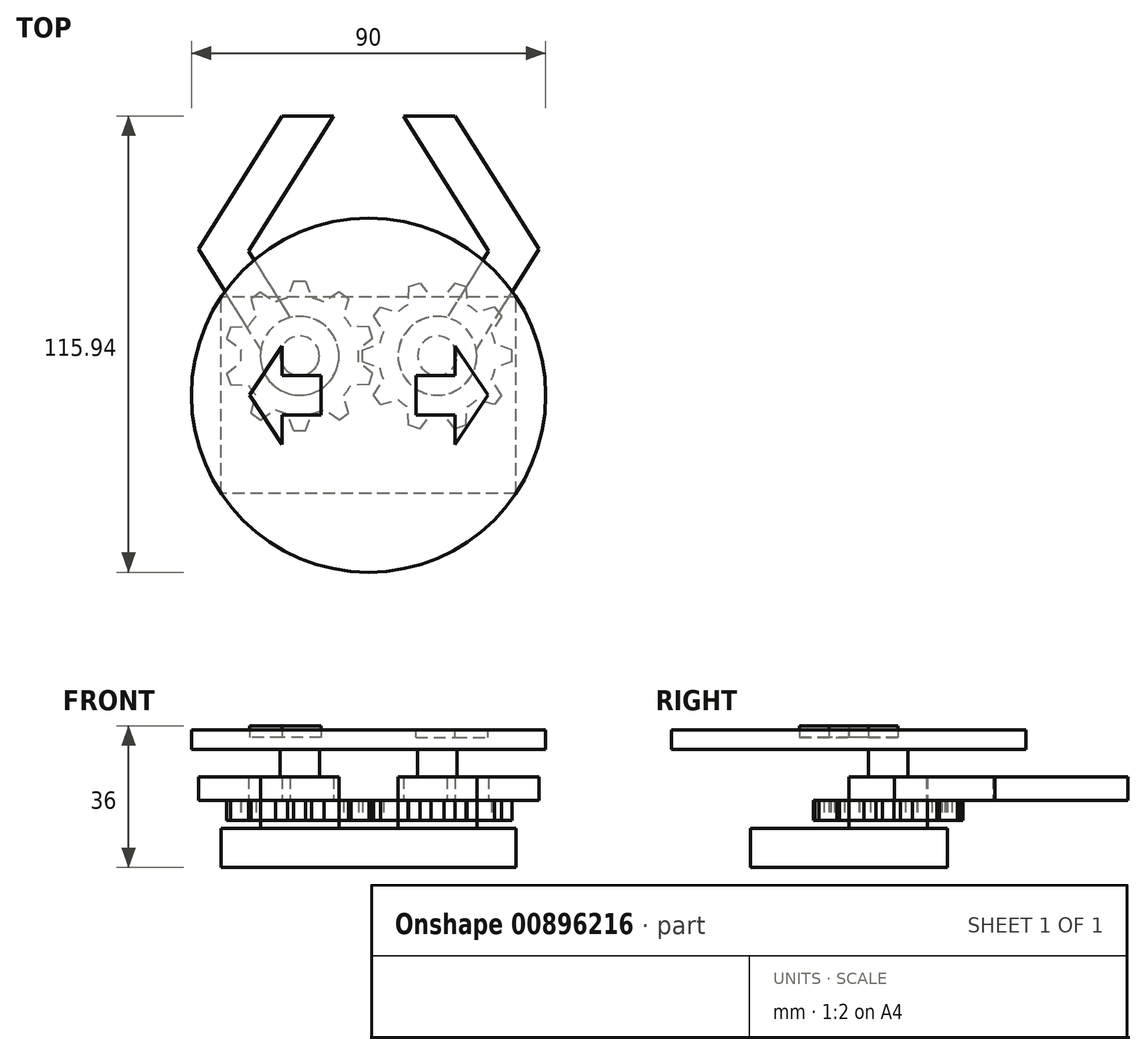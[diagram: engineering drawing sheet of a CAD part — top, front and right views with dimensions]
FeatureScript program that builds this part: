
annotation { "Feature Type Name" : "Feature", "Feature Type Description" : "" }
export const myFeature = defineFeature(function(context is Context, id is Id, definition is map)
    precondition{}
    {
        {
            var Q0;
            Q0=qCreatedBy(makeId("Top.planeOp"),FACE);
            var sketch = newSketch(context, id + "F0", { "sketchPlane" : qUnion([Q0])});
            skLineSegment(sketch, "E0.bottom", {"start": v(37.5, -25) * mm, "end": v(-37.5, -25) * mm});
            skLineSegment(sketch, "E0.top", {"start": v(37.5, 25) * mm, "end": v(-37.5, 25) * mm});
            skLineSegment(sketch, "E0.left", {"start": v(37.5, -25) * mm, "end": v(37.5, 25) * mm});
            skLineSegment(sketch, "E0.right", {"start": v(-37.5, -25) * mm, "end": v(-37.5, 25) * mm});
            skPoint(sketch, "E0.middle", {"position": v(0, 0) * mm});
            skSolve(sketch);
        }
        {
            var Q0;
            Q0 = qSketchRegion(id + "F0", true);
            extrude(context, id + "F1", {"entities" : qUnion([Q0]), "depth" : 10 * mm, "offsetDistance" : 25 * mm});
        }
        {
            var Q0;
            Q0=makeQuery(id+"F1.opExtrude","CAP_FACE",FACE,{"disambiguationData":[OSD([sQuery(id+"F0.wireOp",EDGE,"E0.bottom"),sQuery(id+"F0.wireOp",EDGE,"E0.top"),sQuery(id+"F0.wireOp",EDGE,"E0.left"),sQuery(id+"F0.wireOp",EDGE,"E0.right")])],"isStart":false});
            var sketch = newSketch(context, id + "F2", { "sketchPlane" : qUnion([Q0])});
            skPoint(sketch, "E1.centerSnap0", {"position": v(-37.5, 0) * mm});
            skCircle(sketch, "E2", {"center": v(-17.5, 10) * mm, "radius": 10 * mm});
            skCircle(sketch, "E3", {"center": v(-17.5, 10) * mm, "radius": 3.5 * mm});
            skCircle(sketch, "E4", {"center": v(17.5, 10) * mm, "radius": 3.5 * mm});
            skCircle(sketch, "E5", {"center": v(17.5, 10) * mm, "radius": 10 * mm});
            skSolve(sketch);
        }
        {
            var Q0;
            Q0 = qSketchRegion(id + "F2", true);
            extrude(context, id + "F3", {"entities" : qUnion([Q0]), "operationType" : NewBodyOperationType.ADD, "depth" : 2 * mm, "offsetDistance" : 25 * mm});
        }
        {
            var Q0;
            Q0=makeQuery(id+"F3.boolean.opBoolean","SPLIT",FACE,{"disambiguationData":[TD([makeQuery(id+"F3.opExtrude","SWEPT_FACE",FACE,{"disambiguationData":[OSD([sQuery(id+"F2.wireOp",EDGE,"E3")])]})])],"derivedFrom":makeQuery(id+"F1.opExtrude","CAP_FACE",FACE,{"disambiguationData":[OSD([sQuery(id+"F0.wireOp",EDGE,"E0.bottom"),sQuery(id+"F0.wireOp",EDGE,"E0.top"),sQuery(id+"F0.wireOp",EDGE,"E0.left"),sQuery(id+"F0.wireOp",EDGE,"E0.right")])],"isStart":false})});
            extrude(context, id + "F4", {"entities" : qUnion([Q0]), "depth" : 20 * mm, "offsetDistance" : 25 * mm});
        }
        {
            var Q0;
            Q0=makeQuery(id+"F3.boolean.opBoolean","SPLIT",FACE,{"disambiguationData":[TD([makeQuery(id+"F3.opExtrude","SWEPT_FACE",FACE,{"disambiguationData":[OSD([sQuery(id+"F2.wireOp",EDGE,"E4")])]})])],"derivedFrom":makeQuery(id+"F1.opExtrude","CAP_FACE",FACE,{"disambiguationData":[OSD([sQuery(id+"F0.wireOp",EDGE,"E0.bottom"),sQuery(id+"F0.wireOp",EDGE,"E0.top"),sQuery(id+"F0.wireOp",EDGE,"E0.left"),sQuery(id+"F0.wireOp",EDGE,"E0.right")])],"isStart":false})});
            extrude(context, id + "F5", {"entities" : qUnion([Q0]), "depth" : 20 * mm, "offsetDistance" : 25 * mm});
        }
        {
            var Q0;
            Q0=makeQuery(id+"F3.opExtrude","CAP_FACE",FACE,{"disambiguationData":[OSD([sQuery(id+"F2.wireOp",EDGE,"E2"),sQuery(id+"F2.wireOp",EDGE,"E3")])],"isStart":false});
            var sketch = newSketch(context, id + "F6", { "sketchPlane" : qUnion([Q0])});
            skCircle(sketch, "E6", {"center": v(-17.5, 10) * mm, "radius": 15 * mm});
            skLineSegment(sketch, "E7", {"start": v(-17.5, 10) * mm, "end": v(-17.5, 25) * mm, "construction": true});
            skLineSegment(sketch, "E8", {"start": v(-17.5, 29) * mm, "end": v(-16, 29) * mm});
            skLineSegment(sketch, "E9", {"start": v(-16, 29) * mm, "end": v(-14.43, 24.68) * mm});
            skLineSegment(sketch, "E10.MirrorCS", {"start": v(-17.5, 29) * mm, "end": v(-19, 29) * mm});
            skLineSegment(sketch, "E11.MirrorCS", {"start": v(-19, 29) * mm, "end": v(-20.57, 24.68) * mm});
            skLineSegment(sketch, "E12.1.0", {"start": v(-29.88, 24.49) * mm, "end": v(-28.61, 20.07) * mm});
            skLineSegment(sketch, "E12.1.1", {"start": v(-28.67, 25.37) * mm, "end": v(-29.88, 24.49) * mm});
            skLineSegment(sketch, "E12.1.2", {"start": v(-28.67, 25.37) * mm, "end": v(-27.45, 26.25) * mm});
            skLineSegment(sketch, "E12.1.3", {"start": v(-27.45, 26.25) * mm, "end": v(-23.64, 23.68) * mm});
            skLineSegment(sketch, "E12.2.0", {"start": v(-36.03, 14.44) * mm, "end": v(-32.41, 11.62) * mm});
            skLineSegment(sketch, "E12.2.1", {"start": v(-35.57, 15.87) * mm, "end": v(-36.03, 14.44) * mm});
            skLineSegment(sketch, "E12.2.2", {"start": v(-35.57, 15.87) * mm, "end": v(-35.1, 17.3) * mm});
            skLineSegment(sketch, "E12.2.3", {"start": v(-35.1, 17.3) * mm, "end": v(-30.51, 17.46) * mm});
            skLineSegment(sketch, "E13.2.3.0", {"start": v(-35.1, 2.7) * mm, "end": v(-30.51, 2.54) * mm});
            skLineSegment(sketch, "E13.3.3.0", {"start": v(-35.57, 4.13) * mm, "end": v(-35.1, 2.7) * mm});
            skLineSegment(sketch, "E13.6.3.0", {"start": v(-35.57, 4.13) * mm, "end": v(-36.03, 5.56) * mm});
            skLineSegment(sketch, "E13.9.3.0", {"start": v(-36.03, 5.56) * mm, "end": v(-32.41, 8.38) * mm});
            skLineSegment(sketch, "E13.2.4.0", {"start": v(-27.45, -6.25) * mm, "end": v(-23.64, -3.68) * mm});
            skLineSegment(sketch, "E13.3.4.0", {"start": v(-28.67, -5.37) * mm, "end": v(-27.45, -6.25) * mm});
            skLineSegment(sketch, "E13.6.4.0", {"start": v(-28.67, -5.37) * mm, "end": v(-29.88, -4.49) * mm});
            skLineSegment(sketch, "E13.9.4.0", {"start": v(-29.88, -4.49) * mm, "end": v(-28.61, -0.07) * mm});
            skLineSegment(sketch, "E14.2.5.0", {"start": v(-16, -9) * mm, "end": v(-14.43, -4.68) * mm});
            skLineSegment(sketch, "E14.3.5.0", {"start": v(-17.5, -9) * mm, "end": v(-16, -9) * mm});
            skLineSegment(sketch, "E14.6.5.0", {"start": v(-17.5, -9) * mm, "end": v(-19, -9) * mm});
            skLineSegment(sketch, "E14.9.5.0", {"start": v(-19, -9) * mm, "end": v(-20.57, -4.68) * mm});
            skLineSegment(sketch, "E14.2.6.0", {"start": v(-5.12, -4.49) * mm, "end": v(-6.39, -0.07) * mm});
            skLineSegment(sketch, "E14.3.6.0", {"start": v(-6.33, -5.37) * mm, "end": v(-5.12, -4.49) * mm});
            skLineSegment(sketch, "E14.6.6.0", {"start": v(-6.33, -5.37) * mm, "end": v(-7.55, -6.25) * mm});
            skLineSegment(sketch, "E14.9.6.0", {"start": v(-7.55, -6.25) * mm, "end": v(-11.36, -3.68) * mm});
            skLineSegment(sketch, "E14.2.7.0", {"start": v(1.03, 5.56) * mm, "end": v(-2.59, 8.38) * mm});
            skLineSegment(sketch, "E14.3.7.0", {"start": v(0.57, 4.13) * mm, "end": v(1.03, 5.56) * mm});
            skLineSegment(sketch, "E14.6.7.0", {"start": v(0.57, 4.13) * mm, "end": v(0.1, 2.7) * mm});
            skLineSegment(sketch, "E14.9.7.0", {"start": v(0.1, 2.7) * mm, "end": v(-4.49, 2.54) * mm});
            skLineSegment(sketch, "E14.2.8.0", {"start": v(0.1, 17.3) * mm, "end": v(-4.49, 17.46) * mm});
            skLineSegment(sketch, "E14.3.8.0", {"start": v(0.57, 15.87) * mm, "end": v(0.1, 17.3) * mm});
            skLineSegment(sketch, "E14.6.8.0", {"start": v(0.57, 15.87) * mm, "end": v(1.03, 14.44) * mm});
            skLineSegment(sketch, "E14.9.8.0", {"start": v(1.03, 14.44) * mm, "end": v(-2.59, 11.62) * mm});
            skLineSegment(sketch, "E14.2.9.0", {"start": v(-7.55, 26.25) * mm, "end": v(-11.36, 23.68) * mm});
            skLineSegment(sketch, "E14.3.9.0", {"start": v(-6.33, 25.37) * mm, "end": v(-7.55, 26.25) * mm});
            skLineSegment(sketch, "E14.6.9.0", {"start": v(-6.33, 25.37) * mm, "end": v(-5.12, 24.49) * mm});
            skLineSegment(sketch, "E14.9.9.0", {"start": v(-5.12, 24.49) * mm, "end": v(-6.39, 20.07) * mm});
            skSolve(sketch);
        }
        {
            var Q0;
            Q0 = qSketchRegion(id + "F6", true);
            extrude(context, id + "F7", {"entities" : qUnion([Q0]), "operationType" : NewBodyOperationType.ADD, "depth" : 5 * mm, "offsetDistance" : 25 * mm});
        }
        {
            var Q0;
            Q0=makeQuery(id+"F3.opExtrude","CAP_FACE",FACE,{"disambiguationData":[OSD([sQuery(id+"F2.wireOp",EDGE,"E4"),sQuery(id+"F2.wireOp",EDGE,"E5")])],"isStart":false});
            var sketch = newSketch(context, id + "F8", { "sketchPlane" : qUnion([Q0])});
            skCircle(sketch, "E15", {"center": v(17.5, 10) * mm, "radius": 15 * mm});
            skLineSegment(sketch, "E16", {"start": v(17.5, 10) * mm, "end": v(2.5, 10) * mm, "construction": true});
            skLineSegment(sketch, "E17", {"start": v(-1.5, 10) * mm, "end": v(-1.5, 11.5) * mm});
            skLineSegment(sketch, "E18", {"start": v(-1.5, 11.5) * mm, "end": v(2.82, 13.07) * mm});
            skLineSegment(sketch, "E19.MirrorCS", {"start": v(-1.5, 10) * mm, "end": v(-1.5, 8.5) * mm});
            skLineSegment(sketch, "E20.MirrorCS", {"start": v(-1.5, 8.5) * mm, "end": v(2.82, 6.93) * mm});
            skLineSegment(sketch, "E21.1.0", {"start": v(2.13, -1.17) * mm, "end": v(1.25, 0.05) * mm});
            skLineSegment(sketch, "E21.1.1", {"start": v(1.25, 0.05) * mm, "end": v(3.82, 3.86) * mm});
            skLineSegment(sketch, "E21.1.2", {"start": v(2.13, -1.17) * mm, "end": v(3.01, -2.38) * mm});
            skLineSegment(sketch, "E21.1.3", {"start": v(3.01, -2.38) * mm, "end": v(7.43, -1.11) * mm});
            skLineSegment(sketch, "E21.2.0", {"start": v(11.63, -8.07) * mm, "end": v(10.2, -7.6) * mm});
            skLineSegment(sketch, "E21.2.1", {"start": v(10.2, -7.6) * mm, "end": v(10.04, -3.01) * mm});
            skLineSegment(sketch, "E21.2.2", {"start": v(11.63, -8.07) * mm, "end": v(13.06, -8.53) * mm});
            skLineSegment(sketch, "E21.2.3", {"start": v(13.06, -8.53) * mm, "end": v(15.88, -4.91) * mm});
            skLineSegment(sketch, "E22.1.3.0", {"start": v(23.37, -8.07) * mm, "end": v(21.94, -8.53) * mm});
            skLineSegment(sketch, "E22.3.3.0", {"start": v(21.94, -8.53) * mm, "end": v(19.12, -4.91) * mm});
            skLineSegment(sketch, "E22.6.3.0", {"start": v(23.37, -8.07) * mm, "end": v(24.8, -7.6) * mm});
            skLineSegment(sketch, "E22.9.3.0", {"start": v(24.8, -7.6) * mm, "end": v(24.96, -3.01) * mm});
            skLineSegment(sketch, "E22.1.4.0", {"start": v(32.87, -1.17) * mm, "end": v(31.99, -2.38) * mm});
            skLineSegment(sketch, "E22.3.4.0", {"start": v(31.99, -2.38) * mm, "end": v(27.57, -1.11) * mm});
            skLineSegment(sketch, "E22.6.4.0", {"start": v(32.87, -1.17) * mm, "end": v(33.75, 0.05) * mm});
            skLineSegment(sketch, "E22.9.4.0", {"start": v(33.75, 0.05) * mm, "end": v(31.18, 3.86) * mm});
            skLineSegment(sketch, "E22.1.5.0", {"start": v(36.5, 10) * mm, "end": v(36.5, 8.5) * mm});
            skLineSegment(sketch, "E22.3.5.0", {"start": v(36.5, 8.5) * mm, "end": v(32.18, 6.93) * mm});
            skLineSegment(sketch, "E22.6.5.0", {"start": v(36.5, 10) * mm, "end": v(36.5, 11.5) * mm});
            skLineSegment(sketch, "E22.9.5.0", {"start": v(36.5, 11.5) * mm, "end": v(32.18, 13.07) * mm});
            skLineSegment(sketch, "E22.1.6.0", {"start": v(32.87, 21.17) * mm, "end": v(33.75, 19.95) * mm});
            skLineSegment(sketch, "E22.3.6.0", {"start": v(33.75, 19.95) * mm, "end": v(31.18, 16.14) * mm});
            skLineSegment(sketch, "E22.6.6.0", {"start": v(32.87, 21.17) * mm, "end": v(31.99, 22.38) * mm});
            skLineSegment(sketch, "E22.9.6.0", {"start": v(31.99, 22.38) * mm, "end": v(27.57, 21.11) * mm});
            skLineSegment(sketch, "E22.1.7.0", {"start": v(23.37, 28.07) * mm, "end": v(24.8, 27.6) * mm});
            skLineSegment(sketch, "E22.3.7.0", {"start": v(24.8, 27.6) * mm, "end": v(24.96, 23.01) * mm});
            skLineSegment(sketch, "E22.6.7.0", {"start": v(23.37, 28.07) * mm, "end": v(21.94, 28.53) * mm});
            skLineSegment(sketch, "E22.9.7.0", {"start": v(21.94, 28.53) * mm, "end": v(19.12, 24.91) * mm});
            skLineSegment(sketch, "E22.1.8.0", {"start": v(11.63, 28.07) * mm, "end": v(13.06, 28.53) * mm});
            skLineSegment(sketch, "E22.3.8.0", {"start": v(13.06, 28.53) * mm, "end": v(15.88, 24.91) * mm});
            skLineSegment(sketch, "E22.6.8.0", {"start": v(11.63, 28.07) * mm, "end": v(10.2, 27.6) * mm});
            skLineSegment(sketch, "E22.9.8.0", {"start": v(10.2, 27.6) * mm, "end": v(10.04, 23.01) * mm});
            skLineSegment(sketch, "E22.1.9.0", {"start": v(2.13, 21.17) * mm, "end": v(3.01, 22.38) * mm});
            skLineSegment(sketch, "E22.3.9.0", {"start": v(3.01, 22.38) * mm, "end": v(7.43, 21.11) * mm});
            skLineSegment(sketch, "E22.6.9.0", {"start": v(2.13, 21.17) * mm, "end": v(1.25, 19.95) * mm});
            skLineSegment(sketch, "E22.9.9.0", {"start": v(1.25, 19.95) * mm, "end": v(3.82, 16.14) * mm});
            skSolve(sketch);
        }
        {
            var Q0;
            Q0 = qSketchRegion(id + "F8", true);
            extrude(context, id + "F9", {"entities" : qUnion([Q0]), "operationType" : NewBodyOperationType.ADD, "depth" : 5 * mm, "offsetDistance" : 25 * mm});
        }
        {
            var Q0;
            Q0=makeQuery(id+"F7.opExtrude","CAP_FACE",FACE,{"disambiguationData":[OSD([sQuery(id+"F6.wireOp",EDGE,"E6"),sQuery(id+"F6.wireOp",EDGE,"E8"),sQuery(id+"F6.wireOp",EDGE,"E9"),sQuery(id+"F6.wireOp",EDGE,"E10.MirrorCS"),sQuery(id+"F6.wireOp",EDGE,"E11.MirrorCS"),sQuery(id+"F6.wireOp",EDGE,"E12.1.0"),sQuery(id+"F6.wireOp",EDGE,"E12.1.1"),sQuery(id+"F6.wireOp",EDGE,"E12.1.2"),sQuery(id+"F6.wireOp",EDGE,"E12.1.3"),sQuery(id+"F6.wireOp",EDGE,"E12.2.0"),sQuery(id+"F6.wireOp",EDGE,"E12.2.1"),sQuery(id+"F6.wireOp",EDGE,"E12.2.2"),sQuery(id+"F6.wireOp",EDGE,"E12.2.3"),sQuery(id+"F6.wireOp",EDGE,"E13.2.3.0"),sQuery(id+"F6.wireOp",EDGE,"E13.3.3.0"),sQuery(id+"F6.wireOp",EDGE,"E13.6.3.0"),sQuery(id+"F6.wireOp",EDGE,"E13.9.3.0"),sQuery(id+"F6.wireOp",EDGE,"E13.2.4.0"),sQuery(id+"F6.wireOp",EDGE,"E13.3.4.0"),sQuery(id+"F6.wireOp",EDGE,"E13.6.4.0"),sQuery(id+"F6.wireOp",EDGE,"E13.9.4.0"),sQuery(id+"F6.wireOp",EDGE,"E14.2.5.0"),sQuery(id+"F6.wireOp",EDGE,"E14.3.5.0"),sQuery(id+"F6.wireOp",EDGE,"E14.6.5.0"),sQuery(id+"F6.wireOp",EDGE,"E14.9.5.0"),sQuery(id+"F6.wireOp",EDGE,"E14.2.6.0"),sQuery(id+"F6.wireOp",EDGE,"E14.3.6.0"),sQuery(id+"F6.wireOp",EDGE,"E14.6.6.0"),sQuery(id+"F6.wireOp",EDGE,"E14.9.6.0"),sQuery(id+"F6.wireOp",EDGE,"E14.2.7.0"),sQuery(id+"F6.wireOp",EDGE,"E14.3.7.0"),sQuery(id+"F6.wireOp",EDGE,"E14.6.7.0"),sQuery(id+"F6.wireOp",EDGE,"E14.9.7.0"),sQuery(id+"F6.wireOp",EDGE,"E14.2.8.0"),sQuery(id+"F6.wireOp",EDGE,"E14.3.8.0"),sQuery(id+"F6.wireOp",EDGE,"E14.6.8.0"),sQuery(id+"F6.wireOp",EDGE,"E14.9.8.0"),sQuery(id+"F6.wireOp",EDGE,"E14.2.9.0"),sQuery(id+"F6.wireOp",EDGE,"E14.3.9.0"),sQuery(id+"F6.wireOp",EDGE,"E14.6.9.0"),sQuery(id+"F6.wireOp",EDGE,"E14.9.9.0")])],"isStart":false});
            var sketch = newSketch(context, id + "F10", { "sketchPlane" : qUnion([Q0])});
            skCircle(sketch, "E23.0", {"center": v(-17.5, 10) * mm, "radius": 3.5 * mm});
            skCircle(sketch, "E24.0", {"center": v(-17.5, 10) * mm, "radius": 10 * mm});
            skLineSegment(sketch, "E25", {"start": v(-27.36, 11.64) * mm, "end": v(-43.25, 37.1) * mm});
            skLineSegment(sketch, "E26", {"start": v(-43.25, 37.1) * mm, "end": v(-21.93, 70.94) * mm});
            skLineSegment(sketch, "E27", {"start": v(-21.93, 70.94) * mm, "end": v(-8.93, 70.94) * mm});
            skLineSegment(sketch, "E28", {"start": v(-8.93, 70.94) * mm, "end": v(-30.51, 36.67) * mm});
            skLineSegment(sketch, "E29", {"start": v(-30.51, 36.67) * mm, "end": v(-19.93, 19.7) * mm});
            skSolve(sketch);
        }
        {
            var Q0;
            Q0 = qSketchRegion(id + "F10", true);
            extrude(context, id + "F11", {"entities" : qUnion([Q0]), "depth" : 6 * mm, "offsetDistance" : 25 * mm});
        }
        {
            var Q0;
            Q0=makeQuery(id+"F11.opExtrude","SWEPT_BODY",BODY,{"disambiguationData":[OSD([sQuery(id+"F10.wireOp",EDGE,"E23.0"),sQuery(id+"F10.wireOp",EDGE,"E24.0"),sQuery(id+"F10.wireOp",EDGE,"E25"),sQuery(id+"F10.wireOp",EDGE,"E26"),sQuery(id+"F10.wireOp",EDGE,"E27"),sQuery(id+"F10.wireOp",EDGE,"E28"),sQuery(id+"F10.wireOp",EDGE,"E29")])]});
            var Q1;
            Q1=qCreatedBy(makeId("Right.planeOp"),FACE);
            mirror(context, id + "F12", {"entities" : qUnion([Q0]), "mirrorPlane" : qUnion([Q1])});
        }
        {
            var Q0;
            Q0=makeQuery(id+"F4.opExtrude","CAP_FACE",FACE,{"disambiguationData":[OSD([sQuery(id+"F0.wireOp",EDGE,"E0.bottom"),sQuery(id+"F0.wireOp",EDGE,"E0.top"),sQuery(id+"F0.wireOp",EDGE,"E0.left"),sQuery(id+"F0.wireOp",EDGE,"E0.right")])],"isStart":false});
            var sketch = newSketch(context, id + "F13", { "sketchPlane" : qUnion([Q0])});
            skCircle(sketch, "E30", {"center": v(0, 0) * mm, "radius": 45 * mm});
            skSolve(sketch);
        }
        {
            var Q0;
            Q0 = qSketchRegion(id + "F13", true);
            extrude(context, id + "F14", {"entities" : qUnion([Q0]), "depth" : 5 * mm, "offsetDistance" : 25 * mm});
        }
        {
            var Q0;
            Q0=makeQuery(id+"F14.opExtrude","CAP_FACE",FACE,{"disambiguationData":[OSD([sQuery(id+"F13.wireOp",EDGE,"E30")])],"isStart":true});
            var sketch = newSketch(context, id + "F15", { "sketchPlane" : qUnion([Q0])});
            skCircle(sketch, "E31.0", {"center": v(-17.5, -10) * mm, "radius": 3.5 * mm});
            skCircle(sketch, "E32.0", {"center": v(17.5, -10) * mm, "radius": 3.5 * mm});
            skCircle(sketch, "E33", {"center": v(-17.5, -10) * mm, "radius": 5 * mm});
            skCircle(sketch, "E34", {"center": v(17.5, -10) * mm, "radius": 5 * mm});
            skSolve(sketch);
        }
        {
            var Q0;
            Q0=makeQuery(id+"F15.imprint","IMPRINT",FACE,{"disambiguationData":[TD([[makeQuery(id+"F15.imprint","IMPRINT",EDGE,{"derivedFrom":sQuery(id+"F15.wireOp",EDGE,"E31.0")}),-1.0]])]});
            var Q1;
            Q1=makeQuery(id+"F15.imprint","IMPRINT",FACE,{"disambiguationData":[TD([[makeQuery(id+"F15.imprint","IMPRINT",EDGE,{"derivedFrom":sQuery(id+"F15.wireOp",EDGE,"E32.0")}),-1.0]])]});
            extrude(context, id + "F16", {"entities" : qUnion([Q0, Q1]), "operationType" : NewBodyOperationType.ADD, "endBound" : BoundingType.UP_TO_NEXT, "depth" : 4 * mm, "offsetDistance" : 25 * mm});
        }
        {
            var Q0;
            Q0=makeQuery(id+"F14.opExtrude","CAP_FACE",FACE,{"disambiguationData":[OSD([sQuery(id+"F13.wireOp",EDGE,"E30")])],"isStart":false});
            var sketch = newSketch(context, id + "F17", { "sketchPlane" : qUnion([Q0])});
            skLineSegment(sketch, "E35", {"start": v(-12, 0) * mm, "end": v(-12, 5) * mm});
            skLineSegment(sketch, "E36", {"start": v(-12, 5) * mm, "end": v(-22, 5) * mm});
            skLineSegment(sketch, "E37", {"start": v(-22, 5) * mm, "end": v(-22, 12.5) * mm});
            skLineSegment(sketch, "E38", {"start": v(-22, 12.5) * mm, "end": v(-30.3, 0) * mm});
            skLineSegment(sketch, "E39.MirrorCS", {"start": v(-22, -12.5) * mm, "end": v(-30.3, 0) * mm});
            skLineSegment(sketch, "E40.MirrorCS", {"start": v(-22, -5) * mm, "end": v(-22, -12.5) * mm});
            skLineSegment(sketch, "E41.MirrorCS", {"start": v(-12, -5) * mm, "end": v(-22, -5) * mm});
            skLineSegment(sketch, "E42.MirrorCS", {"start": v(-12, 0) * mm, "end": v(-12, -5) * mm});
            skLineSegment(sketch, "E43.MirrorCS", {"start": v(12, 0) * mm, "end": v(12, 5) * mm});
            skLineSegment(sketch, "E44.MirrorCS", {"start": v(12, 0) * mm, "end": v(12, -5) * mm});
            skLineSegment(sketch, "E45.MirrorCS", {"start": v(12, -5) * mm, "end": v(22, -5) * mm});
            skLineSegment(sketch, "E46.MirrorCS", {"start": v(22, -5) * mm, "end": v(22, -12.5) * mm});
            skLineSegment(sketch, "E47.MirrorCS", {"start": v(22, -12.5) * mm, "end": v(30.3, 0) * mm});
            skLineSegment(sketch, "E48.MirrorCS", {"start": v(22, 12.5) * mm, "end": v(30.3, 0) * mm});
            skLineSegment(sketch, "E49.MirrorCS", {"start": v(22, 5) * mm, "end": v(22, 12.5) * mm});
            skLineSegment(sketch, "E50.MirrorCS", {"start": v(12, 5) * mm, "end": v(22, 5) * mm});
            skSolve(sketch);
        }
        {
            var Q0;
            Q0 = qSketchRegion(id + "F17", true);
            extrude(context, id + "F18", {"entities" : qUnion([Q0]), "operationType" : NewBodyOperationType.REMOVE, "oppositeDirection" : true, "depth" : 2 * mm, "offsetDistance" : 25 * mm});
        }
        {
            var Q0;
            Q0=makeQuery(id+"F18.boolean.opBoolean","COPY",FACE,{"derivedFrom":makeQuery(id+"F18.opExtrude","CAP_FACE",FACE,{"disambiguationData":[OSD([sQuery(id+"F17.wireOp",EDGE,"E35"),sQuery(id+"F17.wireOp",EDGE,"E36"),sQuery(id+"F17.wireOp",EDGE,"E37"),sQuery(id+"F17.wireOp",EDGE,"E38"),sQuery(id+"F17.wireOp",EDGE,"E39.MirrorCS"),sQuery(id+"F17.wireOp",EDGE,"E40.MirrorCS"),sQuery(id+"F17.wireOp",EDGE,"E41.MirrorCS"),sQuery(id+"F17.wireOp",EDGE,"E42.MirrorCS")])],"isStart":false})});
            extrude(context, id + "F19", {"entities" : qUnion([Q0]), "depth" : 3 * mm, "offsetDistance" : 25 * mm});
        }
    });
